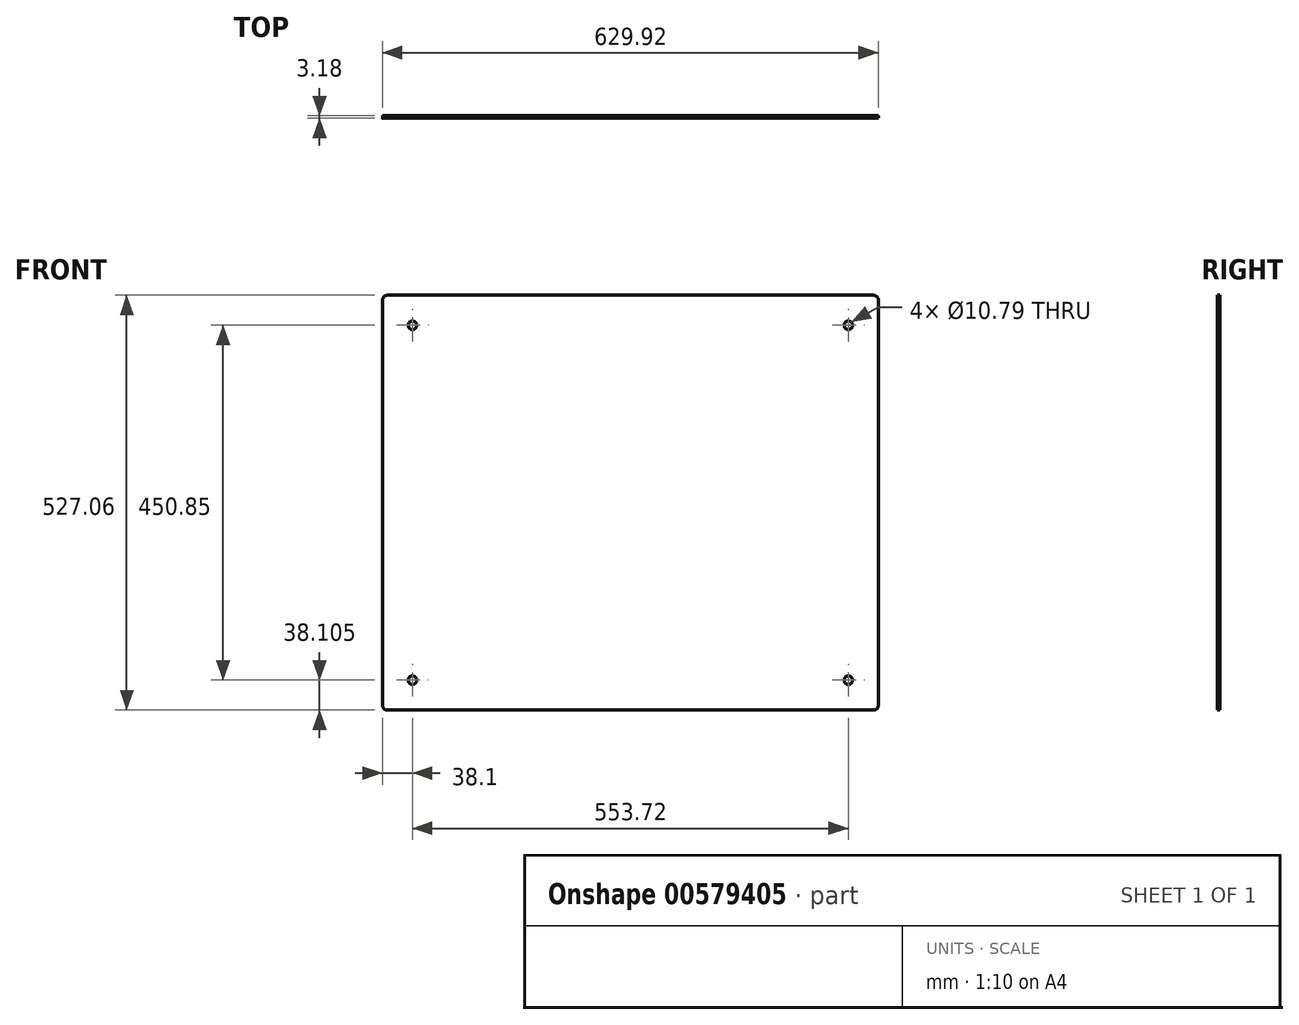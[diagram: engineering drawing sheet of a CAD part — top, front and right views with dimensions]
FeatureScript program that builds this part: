
annotation { "Feature Type Name" : "Feature", "Feature Type Description" : "" }
export const myFeature = defineFeature(function(context is Context, id is Id, definition is map)
    precondition{}
    {
        {
            var Q0;
            Q0=qCreatedBy(makeId("Front.planeOp"),FACE);
            var sketch = newSketch(context, id + "F0", { "sketchPlane" : qUnion([Q0])});
            skLineSegment(sketch, "E0.bottom", {"start": v(308.61, -263.53) * mm, "end": v(-308.6, -263.53) * mm});
            skLineSegment(sketch, "E0.top", {"start": v(308.61, 263.53) * mm, "end": v(-308.6, 263.53) * mm});
            skLineSegment(sketch, "E0.left", {"start": v(314.96, -257.18) * mm, "end": v(314.96, 257.18) * mm});
            skLineSegment(sketch, "E0.right", {"start": v(-314.96, -257.18) * mm, "end": v(-314.96, 257.17) * mm});
            skPoint(sketch, "E0.middle", {"position": v(0, 0) * mm});
            skLineSegment(sketch, "E1.bottom", {"start": v(276.86, -225.43) * mm, "end": v(-276.86, -225.43) * mm, "construction": true});
            skLineSegment(sketch, "E1.top", {"start": v(276.86, 225.43) * mm, "end": v(-276.86, 225.43) * mm, "construction": true});
            skLineSegment(sketch, "E1.left", {"start": v(276.86, -225.43) * mm, "end": v(276.86, 225.43) * mm, "construction": true});
            skLineSegment(sketch, "E1.right", {"start": v(-276.86, -225.43) * mm, "end": v(-276.86, 225.43) * mm, "construction": true});
            skCircle(sketch, "E2", {"center": v(-276.86, 225.43) * mm, "radius": 5.4 * mm});
            skCircle(sketch, "E3", {"center": v(276.86, 225.43) * mm, "radius": 5.4 * mm});
            skCircle(sketch, "E4", {"center": v(276.86, -225.43) * mm, "radius": 5.4 * mm});
            skCircle(sketch, "E5", {"center": v(-276.86, -225.43) * mm, "radius": 5.4 * mm});
            skPoint(sketch, "E6.visualSharp", {"position": v(-314.96, 263.53) * mm});
            skArc(sketch, "E6.filletArc", {"start": v(-308.6, 263.53) * mm, "mid": v(-313.1, 261.67) * mm, "end": v(-314.96, 257.17) * mm});
            skPoint(sketch, "E7.visualSharp", {"position": v(314.96, 263.53) * mm});
            skArc(sketch, "E7.filletArc", {"start": v(314.96, 257.18) * mm, "mid": v(313.1, 261.67) * mm, "end": v(308.61, 263.53) * mm});
            skPoint(sketch, "E8.visualSharp", {"position": v(314.96, -263.53) * mm});
            skArc(sketch, "E8.filletArc", {"start": v(308.61, -263.53) * mm, "mid": v(313.1, -261.67) * mm, "end": v(314.96, -257.18) * mm});
            skPoint(sketch, "E9.visualSharp", {"position": v(-314.96, -263.53) * mm});
            skArc(sketch, "E9.filletArc", {"start": v(-314.96, -257.18) * mm, "mid": v(-313.1, -261.67) * mm, "end": v(-308.6, -263.53) * mm});
            skSolve(sketch);
        }
        {
            var Q0;
            Q0=makeQuery(id+"F0.imprint","IMPRINT",FACE,{"disambiguationData":[TD([[makeQuery(id+"F0.imprint","IMPRINT",EDGE,{"derivedFrom":sQuery(id+"F0.wireOp",EDGE,"E0.bottom")}),-1.0]])]});
            extrude(context, id + "F1", {"entities" : qUnion([Q0]), "depth" : 3.17 * mm, "offsetDistance" : 25.4 * mm});
        }
    });
